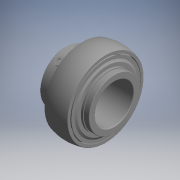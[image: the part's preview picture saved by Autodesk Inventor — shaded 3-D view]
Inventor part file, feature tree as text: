
AUTODESK INVENTOR PART (.ipt)
format: ipt  version: 2017.3 (Build 213256000, 256)  size: 510,464 bytes
history: native  units: mm (DEFAULTED — no unit token found)
features: other x70, sketch x7, revolve x5, extrude x2
ambient origin geometry x8: Origin, YZ Plane, XZ Plane, XY Plane, X Axis, Y Axis, Z Axis, Center Point
bodies: Solid1 (feature_tree)
feature tree (84):
  revolve  "Revolution1"  [1 undecoded]
  extrude  "Extrusion1"  TaperAngle=360.0deg  [1 undecoded]
  extrude  "Extrusion2"  TaperAngle=360.0deg  [1 undecoded]
  sketch  "Sketch_10"  dims[d8=360.0deg]
  sketch  "Sketch_15"
  sketch  "Sketch_16"
  revolve  "Revolution2"  [1 undecoded]
  revolve  "Revolution3"  [1 undecoded]
  revolve  "Revolution4"  [1 undecoded]
  revolve  "Revolution5"  [1 undecoded]
  other  "ball_1_XY"
  other  "ball_1_YZ"
  other  "ball_1_ZX"
  other  "ball_1_X"
  other  "ball_1_Y"
  other  "ball_1_Z"
  other  "ball_1_Center"
  other  "ball_2_XY"
  other  "ball_2_YZ"
  other  "ball_2_ZX"
  other  "ball_2_X"
  other  "ball_2_Y"
  other  "ball_2_Z"
  other  "ball_2_Center"
  other  "ball_3_XY"
  other  "ball_3_YZ"
  other  "ball_3_ZX"
  other  "ball_3_X"
  other  "ball_3_Y"
  other  "ball_3_Z"
  other  "ball_3_Center"
  other  "ball_4_XY"
  other  "ball_4_YZ"
  other  "ball_4_ZX"
  other  "ball_4_X"
  other  "ball_4_Y"
  other  "ball_4_Z"
  other  "ball_4_Center"
  other  "ball_5_XY"
  other  "ball_5_YZ"
  other  "ball_5_ZX"
  other  "ball_5_X"
  other  "ball_5_Y"
  other  "ball_5_Z"
  other  "ball_5_Center"
  other  "ball_6_XY"
  other  "ball_6_YZ"
  other  "ball_6_ZX"
  other  "ball_6_X"
  other  "ball_6_Y"
  other  "ball_6_Z"
  other  "ball_6_Center"
  other  "ball_7_XY"
  other  "ball_7_YZ"
  other  "ball_7_ZX"
  other  "ball_7_X"
  other  "ball_7_Y"
  other  "ball_7_Z"
  other  "ball_7_Center"
  other  "ball_8_XY"
  other  "ball_8_YZ"
  other  "ball_8_ZX"
  other  "ball_8_X"
  other  "ball_8_Y"
  other  "ball_8_Z"
  other  "ball_8_Center"
  other  "ball_9_XY"
  other  "ball_9_YZ"
  other  "ball_9_ZX"
  other  "ball_9_X"
  other  "ball_9_Y"
  other  "ball_9_Z"
  other  "ball_9_Center"
  other  "brg_XY"
  other  "brg_YZ"
  other  "brg_ZX"
  other  "brg_X"
  other  "brg_Y"
  other  "brg_Z"
  other  "brg_Center"
  sketch  "Sketch_1"  dims[d0=360.0deg d1=5.335mm d2=0.0mm]
  sketch  "Sketch_2"  dims[d3=5.335mm d4=0.0mm d5=360.0deg]
  sketch  "Sketch_3"  dims[d6=360.0deg d7=360.0deg]
  sketch  "Sketch_21"
note: 7 required parameter values undecoded (feature->parameter linkage not recoverable at this tier; creation-order binding heuristic only, values carry confidence <= 0.55)